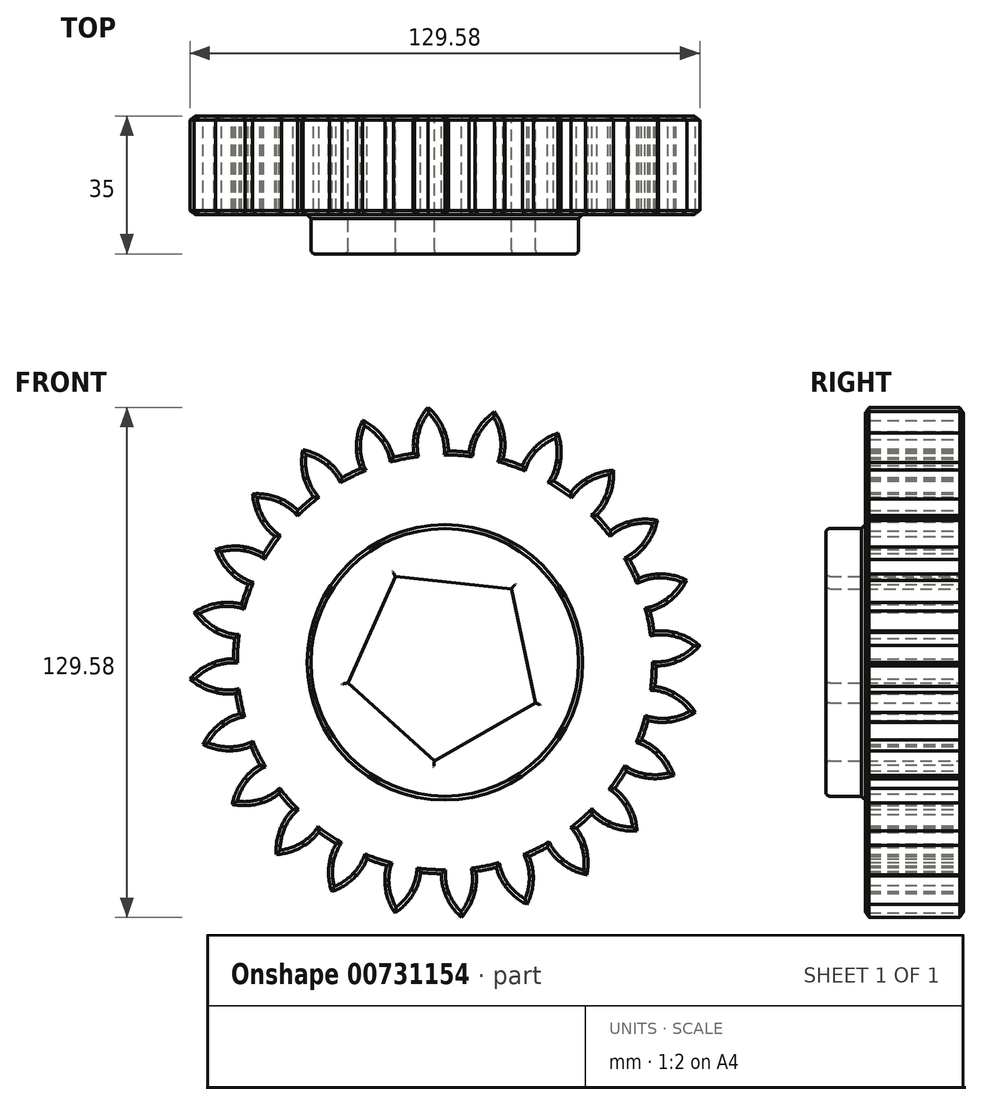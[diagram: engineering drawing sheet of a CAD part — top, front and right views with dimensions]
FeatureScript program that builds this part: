
annotation { "Feature Type Name" : "Feature", "Feature Type Description" : "" }
export const myFeature = defineFeature(function(context is Context, id is Id, definition is map)
    precondition{}
    {
        {
            var Q0;
            Q0=qCreatedBy(makeId("Front.planeOp"),FACE);
            var sketch = newSketch(context, id + "F0", { "sketchPlane" : qUnion([Q0])});
            skCircle(sketch, "E0", {"center": v(0, 0) * mm, "radius": 63.5 * mm, "construction": true});
            skCircle(sketch, "E1", {"center": v(0, 0) * mm, "radius": 58.67 * mm, "construction": true});
            skCircle(sketch, "E2", {"center": v(0, 0) * mm, "radius": 53.72 * mm});
            skLineSegment(sketch, "E3", {"start": v(0, 0) * mm, "end": v(0, 74.51) * mm, "construction": true});
            skLineSegment(sketch, "E4", {"start": v(0, 0) * mm, "end": v(-4.88, 74.51) * mm, "construction": true});
            skLineSegment(sketch, "E5", {"start": v(0, 58.67) * mm, "end": v(-41.54, 58.67) * mm, "construction": true});
            skLineSegment(sketch, "E6", {"start": v(0, 58.67) * mm, "end": v(-41.54, 43.56) * mm, "construction": true});
            skCircle(sketch, "E7", {"center": v(0, 0) * mm, "radius": 55.14 * mm, "construction": true});
            skCircle(sketch, "E8", {"center": v(0, 58.67) * mm, "radius": 14.6 * mm, "construction": true});
            skCircle(sketch, "E9", {"center": v(-13.72, 53.68) * mm, "radius": 14.6 * mm, "construction": true});
            skArc(sketch, "E10", {"start": v(0, 58.67) * mm, "mid": v(-1.73, 62) * mm, "end": v(-4.25, 64.8) * mm});
            skArc(sketch, "E11.MirrorCS", {"start": v(-7.66, 58.17) * mm, "mid": v(-6.38, 61.7) * mm, "end": v(-4.25, 64.8) * mm});
            skArc(sketch, "E12", {"start": v(0.88, 53.71) * mm, "mid": v(0.67, 56.24) * mm, "end": v(0, 58.67) * mm});
            skArc(sketch, "E13.MirrorCS", {"start": v(-7.88, 53.14) * mm, "mid": v(-8, 55.67) * mm, "end": v(-7.66, 58.17) * mm});
            skCircle(sketch, "E14", {"center": v(0, 0) * mm, "radius": 34 * mm});
            skCircle(sketch, "E15.cCircle", {"center": v(0, 0) * mm, "radius": 20.38 * mm, "construction": true});
            skLineSegment(sketch, "E15.0", {"start": v(-12.57, 21.83) * mm, "end": v(16.88, 18.7) * mm});
            skLineSegment(sketch, "E15.1", {"start": v(16.88, 18.7) * mm, "end": v(23, -10.27) * mm});
            skLineSegment(sketch, "E15.2", {"start": v(23, -10.27) * mm, "end": v(-2.66, -25.05) * mm});
            skLineSegment(sketch, "E15.3", {"start": v(-2.66, -25.05) * mm, "end": v(-24.64, -5.2) * mm});
            skLineSegment(sketch, "E15.4", {"start": v(-24.64, -5.2) * mm, "end": v(-12.57, 21.83) * mm});
            skPoint(sketch, "E15.0.midPoint", {"position": v(2.16, 20.26) * mm});
            skSolve(sketch);
        }
        {
            var Q0;
            Q0=makeQuery(id+"F0.imprint","IMPRINT",FACE,{"disambiguationData":[TD([[makeQuery(id+"F0.imprint","IMPRINT",EDGE,{"derivedFrom":sQuery(id+"F0.wireOp",EDGE,"E10")}),1.0]])]});
            var Q1;
            {var subQ0=sQuery(id+"F0.wireOp",EDGE,"E2");var subQ1=makeQuery(id+"F0.imprint","INTERSECT",VERTEX,{"derivedFrom":[subQ0,sQuery(id+"F0.wireOp",EDGE,"E12")]});Q1=makeQuery(id+"F0.imprint","IMPRINT",FACE,{"disambiguationData":[TD([[makeQuery(id+"F0.imprint","IMPRINT",EDGE,{"disambiguationData":[TD([[subQ1,-1.0]])],"derivedFrom":subQ0}),1.0]])]});}
            extrude(context, id + "F1", {"entities" : qUnion([Q0, Q1]), "depth" : 25 * mm, "offsetDistance" : 25 * mm});
        }
        {
            var Q0;
            Q0=makeQuery(id+"F1.opExtrude","SWEPT_BODY",BODY,{"disambiguationData":[OSD([sQuery(id+"F0.wireOp",EDGE,"E2"),sQuery(id+"F0.wireOp",EDGE,"E10"),sQuery(id+"F0.wireOp",EDGE,"E11.MirrorCS"),sQuery(id+"F0.wireOp",EDGE,"E12"),sQuery(id+"F0.wireOp",EDGE,"E13.MirrorCS")])]});
            var Q1;
            Q1=makeQuery(id+"F1.opExtrude","SWEPT_FACE",FACE,{"disambiguationData":[OSD([sQuery(id+"F0.wireOp",EDGE,"E2")])]});
            circularPattern(context, id + "F2", {"entities" : qUnion([Q0]), "axis" : qUnion([Q1]), "angle" : 360 * degree, "instanceCount" : 24, "equalSpace" : true});
        }
        {
            var Q0;
            Q0=makeQuery(id+"F0.imprint","IMPRINT",FACE,{"disambiguationData":[TD([[makeQuery(id+"F0.imprint","IMPRINT",EDGE,{"derivedFrom":sQuery(id+"F0.wireOp",EDGE,"E14")}),1.0]])]});
            extrude(context, id + "F3", {"entities" : qUnion([Q0]), "operationType" : NewBodyOperationType.ADD, "depth" : 35 * mm, "offsetDistance" : 25 * mm});
        }
        {
            var Q0;
            {var subQ0=makeQuery(id+"F1.opExtrude","CAP_FACE",FACE,{"disambiguationData":[OSD([sQuery(id+"F0.wireOp",EDGE,"E2"),sQuery(id+"F0.wireOp",EDGE,"E10"),sQuery(id+"F0.wireOp",EDGE,"E11.MirrorCS"),sQuery(id+"F0.wireOp",EDGE,"E12"),sQuery(id+"F0.wireOp",EDGE,"E13.MirrorCS"),sQuery(id+"F0.wireOp",EDGE,"E14")])],"isStart":false});Q0=makeQuery(id+"F3.boolean.opBoolean","MERGE",FACE,{"derivedFrom":[subQ0,makeQuery(id+"F2.opPattern","COPY",FACE,{"derivedFrom":subQ0,"instanceName":"1"}),makeQuery(id+"F2.opPattern","COPY",FACE,{"derivedFrom":subQ0,"instanceName":"2"}),makeQuery(id+"F2.opPattern","COPY",FACE,{"derivedFrom":subQ0,"instanceName":"3"}),makeQuery(id+"F2.opPattern","COPY",FACE,{"derivedFrom":subQ0,"instanceName":"4"}),makeQuery(id+"F2.opPattern","COPY",FACE,{"derivedFrom":subQ0,"instanceName":"5"}),makeQuery(id+"F2.opPattern","COPY",FACE,{"derivedFrom":subQ0,"instanceName":"6"}),makeQuery(id+"F2.opPattern","COPY",FACE,{"derivedFrom":subQ0,"instanceName":"7"}),makeQuery(id+"F2.opPattern","COPY",FACE,{"derivedFrom":subQ0,"instanceName":"8"}),makeQuery(id+"F2.opPattern","COPY",FACE,{"derivedFrom":subQ0,"instanceName":"9"}),makeQuery(id+"F2.opPattern","COPY",FACE,{"derivedFrom":subQ0,"instanceName":"10"}),makeQuery(id+"F2.opPattern","COPY",FACE,{"derivedFrom":subQ0,"instanceName":"11"}),makeQuery(id+"F2.opPattern","COPY",FACE,{"derivedFrom":subQ0,"instanceName":"12"}),makeQuery(id+"F2.opPattern","COPY",FACE,{"derivedFrom":subQ0,"instanceName":"13"}),makeQuery(id+"F2.opPattern","COPY",FACE,{"derivedFrom":subQ0,"instanceName":"14"}),makeQuery(id+"F2.opPattern","COPY",FACE,{"derivedFrom":subQ0,"instanceName":"15"}),makeQuery(id+"F2.opPattern","COPY",FACE,{"derivedFrom":subQ0,"instanceName":"16"}),makeQuery(id+"F2.opPattern","COPY",FACE,{"derivedFrom":subQ0,"instanceName":"17"}),makeQuery(id+"F2.opPattern","COPY",FACE,{"derivedFrom":subQ0,"instanceName":"18"}),makeQuery(id+"F2.opPattern","COPY",FACE,{"derivedFrom":subQ0,"instanceName":"19"}),makeQuery(id+"F2.opPattern","COPY",FACE,{"derivedFrom":subQ0,"instanceName":"20"}),makeQuery(id+"F2.opPattern","COPY",FACE,{"derivedFrom":subQ0,"instanceName":"21"}),makeQuery(id+"F2.opPattern","COPY",FACE,{"derivedFrom":subQ0,"instanceName":"22"}),makeQuery(id+"F2.opPattern","COPY",FACE,{"derivedFrom":subQ0,"instanceName":"23"})]});}
            var Q1;
            {var subQ0=sQuery(id+"F0.wireOp",EDGE,"E14");var subQ1=makeQuery(id+"F1.opExtrude","CAP_FACE",FACE,{"disambiguationData":[OSD([sQuery(id+"F0.wireOp",EDGE,"E2"),sQuery(id+"F0.wireOp",EDGE,"E10"),sQuery(id+"F0.wireOp",EDGE,"E11.MirrorCS"),sQuery(id+"F0.wireOp",EDGE,"E12"),sQuery(id+"F0.wireOp",EDGE,"E13.MirrorCS"),subQ0])],"isStart":true});Q1=makeQuery(id+"F3.boolean.opBoolean","MERGE",FACE,{"derivedFrom":[subQ1,makeQuery(id+"F2.opPattern","COPY",FACE,{"derivedFrom":subQ1,"instanceName":"1"}),makeQuery(id+"F2.opPattern","COPY",FACE,{"derivedFrom":subQ1,"instanceName":"2"}),makeQuery(id+"F2.opPattern","COPY",FACE,{"derivedFrom":subQ1,"instanceName":"3"}),makeQuery(id+"F2.opPattern","COPY",FACE,{"derivedFrom":subQ1,"instanceName":"4"}),makeQuery(id+"F2.opPattern","COPY",FACE,{"derivedFrom":subQ1,"instanceName":"5"}),makeQuery(id+"F2.opPattern","COPY",FACE,{"derivedFrom":subQ1,"instanceName":"6"}),makeQuery(id+"F2.opPattern","COPY",FACE,{"derivedFrom":subQ1,"instanceName":"7"}),makeQuery(id+"F2.opPattern","COPY",FACE,{"derivedFrom":subQ1,"instanceName":"8"}),makeQuery(id+"F2.opPattern","COPY",FACE,{"derivedFrom":subQ1,"instanceName":"9"}),makeQuery(id+"F2.opPattern","COPY",FACE,{"derivedFrom":subQ1,"instanceName":"10"}),makeQuery(id+"F2.opPattern","COPY",FACE,{"derivedFrom":subQ1,"instanceName":"11"}),makeQuery(id+"F2.opPattern","COPY",FACE,{"derivedFrom":subQ1,"instanceName":"12"}),makeQuery(id+"F2.opPattern","COPY",FACE,{"derivedFrom":subQ1,"instanceName":"13"}),makeQuery(id+"F2.opPattern","COPY",FACE,{"derivedFrom":subQ1,"instanceName":"14"}),makeQuery(id+"F2.opPattern","COPY",FACE,{"derivedFrom":subQ1,"instanceName":"15"}),makeQuery(id+"F2.opPattern","COPY",FACE,{"derivedFrom":subQ1,"instanceName":"16"}),makeQuery(id+"F2.opPattern","COPY",FACE,{"derivedFrom":subQ1,"instanceName":"17"}),makeQuery(id+"F2.opPattern","COPY",FACE,{"derivedFrom":subQ1,"instanceName":"18"}),makeQuery(id+"F2.opPattern","COPY",FACE,{"derivedFrom":subQ1,"instanceName":"19"}),makeQuery(id+"F2.opPattern","COPY",FACE,{"derivedFrom":subQ1,"instanceName":"20"}),makeQuery(id+"F2.opPattern","COPY",FACE,{"derivedFrom":subQ1,"instanceName":"21"}),makeQuery(id+"F2.opPattern","COPY",FACE,{"derivedFrom":subQ1,"instanceName":"22"}),makeQuery(id+"F2.opPattern","COPY",FACE,{"derivedFrom":subQ1,"instanceName":"23"}),makeQuery(id+"F3.opExtrude","CAP_FACE",FACE,{"disambiguationData":[OSD([subQ0,sQuery(id+"F0.wireOp",EDGE,"E15.0"),sQuery(id+"F0.wireOp",EDGE,"E15.1"),sQuery(id+"F0.wireOp",EDGE,"E15.2"),sQuery(id+"F0.wireOp",EDGE,"E15.3"),sQuery(id+"F0.wireOp",EDGE,"E15.4")])],"isStart":true})]});}
            chamfer(context, id + "F4", {"entities" : qUnion([Q0, Q1]), "width" : 1 * mm, "tangentPropagation" : true});
        }
        {
            var Q0;
            {var subQ0=sQuery(id+"F0.wireOp",EDGE,"E15.1");Q0=makeQuery(id+"F4.opChamfer","BLEND_EDGE",EDGE,{"blendedFrom":[makeQuery(id+"F3.opExtrude","CAP_EDGE",EDGE,{"disambiguationData":[OSD([subQ0])],"isStart":true}),makeQuery(id+"F3.opExtrude","SWEPT_FACE",FACE,{"disambiguationData":[OSD([subQ0])]})],"blendedInto":[makeQuery(id+"F3.opExtrude","SWEPT_FACE",FACE,{"disambiguationData":[OSD([subQ0])]})]});}
            var Q1;
            Q1=makeQuery(id+"F3.opExtrude","CAP_FACE",FACE,{"disambiguationData":[OSD([sQuery(id+"F0.wireOp",EDGE,"E14"),sQuery(id+"F0.wireOp",EDGE,"E15.0"),sQuery(id+"F0.wireOp",EDGE,"E15.1"),sQuery(id+"F0.wireOp",EDGE,"E15.2"),sQuery(id+"F0.wireOp",EDGE,"E15.3"),sQuery(id+"F0.wireOp",EDGE,"E15.4")])],"isStart":false});
            var Q2;
            Q2=makeQuery(id+"F3.opExtrude","CAP_EDGE",EDGE,{"disambiguationData":[OSD([sQuery(id+"F0.wireOp",EDGE,"E15.2")])],"isStart":false});
            var Q3;
            Q3=makeQuery(id+"F3.opExtrude","CAP_EDGE",EDGE,{"disambiguationData":[OSD([sQuery(id+"F0.wireOp",EDGE,"E15.3")])],"isStart":false});
            var Q4;
            Q4=makeQuery(id+"F3.opExtrude","CAP_EDGE",EDGE,{"disambiguationData":[OSD([sQuery(id+"F0.wireOp",EDGE,"E15.4")])],"isStart":false});
            var Q5;
            Q5=makeQuery(id+"F3.opExtrude","CAP_EDGE",EDGE,{"disambiguationData":[OSD([sQuery(id+"F0.wireOp",EDGE,"E15.0")])],"isStart":false});
            var Q6;
            {var subQ0=sQuery(id+"F0.wireOp",EDGE,"E15.4");var subQ1=sQuery(id+"F0.wireOp",EDGE,"E14");var subQ2=makeQuery(id+"F1.opExtrude","CAP_FACE",FACE,{"disambiguationData":[OSD([sQuery(id+"F0.wireOp",EDGE,"E2"),sQuery(id+"F0.wireOp",EDGE,"E10"),sQuery(id+"F0.wireOp",EDGE,"E11.MirrorCS"),sQuery(id+"F0.wireOp",EDGE,"E12"),sQuery(id+"F0.wireOp",EDGE,"E13.MirrorCS"),subQ1])],"isStart":true});Q6=makeQuery(id+"F4.opChamfer","BLEND_EDGE",EDGE,{"blendedFrom":[makeQuery(id+"F3.opExtrude","CAP_EDGE",EDGE,{"disambiguationData":[OSD([subQ0])],"isStart":true}),makeQuery(id+"F3.boolean.opBoolean","MERGE",FACE,{"derivedFrom":[subQ2,makeQuery(id+"F2.opPattern","COPY",FACE,{"derivedFrom":subQ2,"instanceName":"1"}),makeQuery(id+"F2.opPattern","COPY",FACE,{"derivedFrom":subQ2,"instanceName":"2"}),makeQuery(id+"F2.opPattern","COPY",FACE,{"derivedFrom":subQ2,"instanceName":"3"}),makeQuery(id+"F2.opPattern","COPY",FACE,{"derivedFrom":subQ2,"instanceName":"4"}),makeQuery(id+"F2.opPattern","COPY",FACE,{"derivedFrom":subQ2,"instanceName":"5"}),makeQuery(id+"F2.opPattern","COPY",FACE,{"derivedFrom":subQ2,"instanceName":"6"}),makeQuery(id+"F2.opPattern","COPY",FACE,{"derivedFrom":subQ2,"instanceName":"7"}),makeQuery(id+"F2.opPattern","COPY",FACE,{"derivedFrom":subQ2,"instanceName":"8"}),makeQuery(id+"F2.opPattern","COPY",FACE,{"derivedFrom":subQ2,"instanceName":"9"}),makeQuery(id+"F2.opPattern","COPY",FACE,{"derivedFrom":subQ2,"instanceName":"10"}),makeQuery(id+"F2.opPattern","COPY",FACE,{"derivedFrom":subQ2,"instanceName":"11"}),makeQuery(id+"F2.opPattern","COPY",FACE,{"derivedFrom":subQ2,"instanceName":"12"}),makeQuery(id+"F2.opPattern","COPY",FACE,{"derivedFrom":subQ2,"instanceName":"13"}),makeQuery(id+"F2.opPattern","COPY",FACE,{"derivedFrom":subQ2,"instanceName":"14"}),makeQuery(id+"F2.opPattern","COPY",FACE,{"derivedFrom":subQ2,"instanceName":"15"}),makeQuery(id+"F2.opPattern","COPY",FACE,{"derivedFrom":subQ2,"instanceName":"16"}),makeQuery(id+"F2.opPattern","COPY",FACE,{"derivedFrom":subQ2,"instanceName":"17"}),makeQuery(id+"F2.opPattern","COPY",FACE,{"derivedFrom":subQ2,"instanceName":"18"}),makeQuery(id+"F2.opPattern","COPY",FACE,{"derivedFrom":subQ2,"instanceName":"19"}),makeQuery(id+"F2.opPattern","COPY",FACE,{"derivedFrom":subQ2,"instanceName":"20"}),makeQuery(id+"F2.opPattern","COPY",FACE,{"derivedFrom":subQ2,"instanceName":"21"}),makeQuery(id+"F2.opPattern","COPY",FACE,{"derivedFrom":subQ2,"instanceName":"22"}),makeQuery(id+"F2.opPattern","COPY",FACE,{"derivedFrom":subQ2,"instanceName":"23"}),makeQuery(id+"F3.opExtrude","CAP_FACE",FACE,{"disambiguationData":[OSD([subQ1,sQuery(id+"F0.wireOp",EDGE,"E15.0"),sQuery(id+"F0.wireOp",EDGE,"E15.1"),sQuery(id+"F0.wireOp",EDGE,"E15.2"),sQuery(id+"F0.wireOp",EDGE,"E15.3"),subQ0])],"isStart":true})]})],"blendedInto":[makeQuery(id+"F3.boolean.opBoolean","MERGE",FACE,{"derivedFrom":[subQ2,makeQuery(id+"F2.opPattern","COPY",FACE,{"derivedFrom":subQ2,"instanceName":"1"}),makeQuery(id+"F2.opPattern","COPY",FACE,{"derivedFrom":subQ2,"instanceName":"2"}),makeQuery(id+"F2.opPattern","COPY",FACE,{"derivedFrom":subQ2,"instanceName":"3"}),makeQuery(id+"F2.opPattern","COPY",FACE,{"derivedFrom":subQ2,"instanceName":"4"}),makeQuery(id+"F2.opPattern","COPY",FACE,{"derivedFrom":subQ2,"instanceName":"5"}),makeQuery(id+"F2.opPattern","COPY",FACE,{"derivedFrom":subQ2,"instanceName":"6"}),makeQuery(id+"F2.opPattern","COPY",FACE,{"derivedFrom":subQ2,"instanceName":"7"}),makeQuery(id+"F2.opPattern","COPY",FACE,{"derivedFrom":subQ2,"instanceName":"8"}),makeQuery(id+"F2.opPattern","COPY",FACE,{"derivedFrom":subQ2,"instanceName":"9"}),makeQuery(id+"F2.opPattern","COPY",FACE,{"derivedFrom":subQ2,"instanceName":"10"}),makeQuery(id+"F2.opPattern","COPY",FACE,{"derivedFrom":subQ2,"instanceName":"11"}),makeQuery(id+"F2.opPattern","COPY",FACE,{"derivedFrom":subQ2,"instanceName":"12"}),makeQuery(id+"F2.opPattern","COPY",FACE,{"derivedFrom":subQ2,"instanceName":"13"}),makeQuery(id+"F2.opPattern","COPY",FACE,{"derivedFrom":subQ2,"instanceName":"14"}),makeQuery(id+"F2.opPattern","COPY",FACE,{"derivedFrom":subQ2,"instanceName":"15"}),makeQuery(id+"F2.opPattern","COPY",FACE,{"derivedFrom":subQ2,"instanceName":"16"}),makeQuery(id+"F2.opPattern","COPY",FACE,{"derivedFrom":subQ2,"instanceName":"17"}),makeQuery(id+"F2.opPattern","COPY",FACE,{"derivedFrom":subQ2,"instanceName":"18"}),makeQuery(id+"F2.opPattern","COPY",FACE,{"derivedFrom":subQ2,"instanceName":"19"}),makeQuery(id+"F2.opPattern","COPY",FACE,{"derivedFrom":subQ2,"instanceName":"20"}),makeQuery(id+"F2.opPattern","COPY",FACE,{"derivedFrom":subQ2,"instanceName":"21"}),makeQuery(id+"F2.opPattern","COPY",FACE,{"derivedFrom":subQ2,"instanceName":"22"}),makeQuery(id+"F2.opPattern","COPY",FACE,{"derivedFrom":subQ2,"instanceName":"23"}),makeQuery(id+"F3.opExtrude","CAP_FACE",FACE,{"disambiguationData":[OSD([subQ1,sQuery(id+"F0.wireOp",EDGE,"E15.0"),sQuery(id+"F0.wireOp",EDGE,"E15.1"),sQuery(id+"F0.wireOp",EDGE,"E15.2"),sQuery(id+"F0.wireOp",EDGE,"E15.3"),subQ0])],"isStart":true})]})]});}
            var Q7;
            {var subQ0=sQuery(id+"F0.wireOp",EDGE,"E15.0");var subQ1=sQuery(id+"F0.wireOp",EDGE,"E14");var subQ2=makeQuery(id+"F1.opExtrude","CAP_FACE",FACE,{"disambiguationData":[OSD([sQuery(id+"F0.wireOp",EDGE,"E2"),sQuery(id+"F0.wireOp",EDGE,"E10"),sQuery(id+"F0.wireOp",EDGE,"E11.MirrorCS"),sQuery(id+"F0.wireOp",EDGE,"E12"),sQuery(id+"F0.wireOp",EDGE,"E13.MirrorCS"),subQ1])],"isStart":true});Q7=makeQuery(id+"F4.opChamfer","BLEND_EDGE",EDGE,{"blendedFrom":[makeQuery(id+"F3.opExtrude","CAP_EDGE",EDGE,{"disambiguationData":[OSD([subQ0])],"isStart":true}),makeQuery(id+"F3.boolean.opBoolean","MERGE",FACE,{"derivedFrom":[subQ2,makeQuery(id+"F2.opPattern","COPY",FACE,{"derivedFrom":subQ2,"instanceName":"1"}),makeQuery(id+"F2.opPattern","COPY",FACE,{"derivedFrom":subQ2,"instanceName":"2"}),makeQuery(id+"F2.opPattern","COPY",FACE,{"derivedFrom":subQ2,"instanceName":"3"}),makeQuery(id+"F2.opPattern","COPY",FACE,{"derivedFrom":subQ2,"instanceName":"4"}),makeQuery(id+"F2.opPattern","COPY",FACE,{"derivedFrom":subQ2,"instanceName":"5"}),makeQuery(id+"F2.opPattern","COPY",FACE,{"derivedFrom":subQ2,"instanceName":"6"}),makeQuery(id+"F2.opPattern","COPY",FACE,{"derivedFrom":subQ2,"instanceName":"7"}),makeQuery(id+"F2.opPattern","COPY",FACE,{"derivedFrom":subQ2,"instanceName":"8"}),makeQuery(id+"F2.opPattern","COPY",FACE,{"derivedFrom":subQ2,"instanceName":"9"}),makeQuery(id+"F2.opPattern","COPY",FACE,{"derivedFrom":subQ2,"instanceName":"10"}),makeQuery(id+"F2.opPattern","COPY",FACE,{"derivedFrom":subQ2,"instanceName":"11"}),makeQuery(id+"F2.opPattern","COPY",FACE,{"derivedFrom":subQ2,"instanceName":"12"}),makeQuery(id+"F2.opPattern","COPY",FACE,{"derivedFrom":subQ2,"instanceName":"13"}),makeQuery(id+"F2.opPattern","COPY",FACE,{"derivedFrom":subQ2,"instanceName":"14"}),makeQuery(id+"F2.opPattern","COPY",FACE,{"derivedFrom":subQ2,"instanceName":"15"}),makeQuery(id+"F2.opPattern","COPY",FACE,{"derivedFrom":subQ2,"instanceName":"16"}),makeQuery(id+"F2.opPattern","COPY",FACE,{"derivedFrom":subQ2,"instanceName":"17"}),makeQuery(id+"F2.opPattern","COPY",FACE,{"derivedFrom":subQ2,"instanceName":"18"}),makeQuery(id+"F2.opPattern","COPY",FACE,{"derivedFrom":subQ2,"instanceName":"19"}),makeQuery(id+"F2.opPattern","COPY",FACE,{"derivedFrom":subQ2,"instanceName":"20"}),makeQuery(id+"F2.opPattern","COPY",FACE,{"derivedFrom":subQ2,"instanceName":"21"}),makeQuery(id+"F2.opPattern","COPY",FACE,{"derivedFrom":subQ2,"instanceName":"22"}),makeQuery(id+"F2.opPattern","COPY",FACE,{"derivedFrom":subQ2,"instanceName":"23"}),makeQuery(id+"F3.opExtrude","CAP_FACE",FACE,{"disambiguationData":[OSD([subQ1,subQ0,sQuery(id+"F0.wireOp",EDGE,"E15.1"),sQuery(id+"F0.wireOp",EDGE,"E15.2"),sQuery(id+"F0.wireOp",EDGE,"E15.3"),sQuery(id+"F0.wireOp",EDGE,"E15.4")])],"isStart":true})]})],"blendedInto":[makeQuery(id+"F3.boolean.opBoolean","MERGE",FACE,{"derivedFrom":[subQ2,makeQuery(id+"F2.opPattern","COPY",FACE,{"derivedFrom":subQ2,"instanceName":"1"}),makeQuery(id+"F2.opPattern","COPY",FACE,{"derivedFrom":subQ2,"instanceName":"2"}),makeQuery(id+"F2.opPattern","COPY",FACE,{"derivedFrom":subQ2,"instanceName":"3"}),makeQuery(id+"F2.opPattern","COPY",FACE,{"derivedFrom":subQ2,"instanceName":"4"}),makeQuery(id+"F2.opPattern","COPY",FACE,{"derivedFrom":subQ2,"instanceName":"5"}),makeQuery(id+"F2.opPattern","COPY",FACE,{"derivedFrom":subQ2,"instanceName":"6"}),makeQuery(id+"F2.opPattern","COPY",FACE,{"derivedFrom":subQ2,"instanceName":"7"}),makeQuery(id+"F2.opPattern","COPY",FACE,{"derivedFrom":subQ2,"instanceName":"8"}),makeQuery(id+"F2.opPattern","COPY",FACE,{"derivedFrom":subQ2,"instanceName":"9"}),makeQuery(id+"F2.opPattern","COPY",FACE,{"derivedFrom":subQ2,"instanceName":"10"}),makeQuery(id+"F2.opPattern","COPY",FACE,{"derivedFrom":subQ2,"instanceName":"11"}),makeQuery(id+"F2.opPattern","COPY",FACE,{"derivedFrom":subQ2,"instanceName":"12"}),makeQuery(id+"F2.opPattern","COPY",FACE,{"derivedFrom":subQ2,"instanceName":"13"}),makeQuery(id+"F2.opPattern","COPY",FACE,{"derivedFrom":subQ2,"instanceName":"14"}),makeQuery(id+"F2.opPattern","COPY",FACE,{"derivedFrom":subQ2,"instanceName":"15"}),makeQuery(id+"F2.opPattern","COPY",FACE,{"derivedFrom":subQ2,"instanceName":"16"}),makeQuery(id+"F2.opPattern","COPY",FACE,{"derivedFrom":subQ2,"instanceName":"17"}),makeQuery(id+"F2.opPattern","COPY",FACE,{"derivedFrom":subQ2,"instanceName":"18"}),makeQuery(id+"F2.opPattern","COPY",FACE,{"derivedFrom":subQ2,"instanceName":"19"}),makeQuery(id+"F2.opPattern","COPY",FACE,{"derivedFrom":subQ2,"instanceName":"20"}),makeQuery(id+"F2.opPattern","COPY",FACE,{"derivedFrom":subQ2,"instanceName":"21"}),makeQuery(id+"F2.opPattern","COPY",FACE,{"derivedFrom":subQ2,"instanceName":"22"}),makeQuery(id+"F2.opPattern","COPY",FACE,{"derivedFrom":subQ2,"instanceName":"23"}),makeQuery(id+"F3.opExtrude","CAP_FACE",FACE,{"disambiguationData":[OSD([subQ1,subQ0,sQuery(id+"F0.wireOp",EDGE,"E15.1"),sQuery(id+"F0.wireOp",EDGE,"E15.2"),sQuery(id+"F0.wireOp",EDGE,"E15.3"),sQuery(id+"F0.wireOp",EDGE,"E15.4")])],"isStart":true})]})]});}
            var Q8;
            {var subQ0=sQuery(id+"F0.wireOp",EDGE,"E15.1");var subQ1=sQuery(id+"F0.wireOp",EDGE,"E14");var subQ2=makeQuery(id+"F1.opExtrude","CAP_FACE",FACE,{"disambiguationData":[OSD([sQuery(id+"F0.wireOp",EDGE,"E2"),sQuery(id+"F0.wireOp",EDGE,"E10"),sQuery(id+"F0.wireOp",EDGE,"E11.MirrorCS"),sQuery(id+"F0.wireOp",EDGE,"E12"),sQuery(id+"F0.wireOp",EDGE,"E13.MirrorCS"),subQ1])],"isStart":true});Q8=makeQuery(id+"F4.opChamfer","BLEND_EDGE",EDGE,{"blendedFrom":[makeQuery(id+"F3.opExtrude","CAP_EDGE",EDGE,{"disambiguationData":[OSD([subQ0])],"isStart":true}),makeQuery(id+"F3.boolean.opBoolean","MERGE",FACE,{"derivedFrom":[subQ2,makeQuery(id+"F2.opPattern","COPY",FACE,{"derivedFrom":subQ2,"instanceName":"1"}),makeQuery(id+"F2.opPattern","COPY",FACE,{"derivedFrom":subQ2,"instanceName":"2"}),makeQuery(id+"F2.opPattern","COPY",FACE,{"derivedFrom":subQ2,"instanceName":"3"}),makeQuery(id+"F2.opPattern","COPY",FACE,{"derivedFrom":subQ2,"instanceName":"4"}),makeQuery(id+"F2.opPattern","COPY",FACE,{"derivedFrom":subQ2,"instanceName":"5"}),makeQuery(id+"F2.opPattern","COPY",FACE,{"derivedFrom":subQ2,"instanceName":"6"}),makeQuery(id+"F2.opPattern","COPY",FACE,{"derivedFrom":subQ2,"instanceName":"7"}),makeQuery(id+"F2.opPattern","COPY",FACE,{"derivedFrom":subQ2,"instanceName":"8"}),makeQuery(id+"F2.opPattern","COPY",FACE,{"derivedFrom":subQ2,"instanceName":"9"}),makeQuery(id+"F2.opPattern","COPY",FACE,{"derivedFrom":subQ2,"instanceName":"10"}),makeQuery(id+"F2.opPattern","COPY",FACE,{"derivedFrom":subQ2,"instanceName":"11"}),makeQuery(id+"F2.opPattern","COPY",FACE,{"derivedFrom":subQ2,"instanceName":"12"}),makeQuery(id+"F2.opPattern","COPY",FACE,{"derivedFrom":subQ2,"instanceName":"13"}),makeQuery(id+"F2.opPattern","COPY",FACE,{"derivedFrom":subQ2,"instanceName":"14"}),makeQuery(id+"F2.opPattern","COPY",FACE,{"derivedFrom":subQ2,"instanceName":"15"}),makeQuery(id+"F2.opPattern","COPY",FACE,{"derivedFrom":subQ2,"instanceName":"16"}),makeQuery(id+"F2.opPattern","COPY",FACE,{"derivedFrom":subQ2,"instanceName":"17"}),makeQuery(id+"F2.opPattern","COPY",FACE,{"derivedFrom":subQ2,"instanceName":"18"}),makeQuery(id+"F2.opPattern","COPY",FACE,{"derivedFrom":subQ2,"instanceName":"19"}),makeQuery(id+"F2.opPattern","COPY",FACE,{"derivedFrom":subQ2,"instanceName":"20"}),makeQuery(id+"F2.opPattern","COPY",FACE,{"derivedFrom":subQ2,"instanceName":"21"}),makeQuery(id+"F2.opPattern","COPY",FACE,{"derivedFrom":subQ2,"instanceName":"22"}),makeQuery(id+"F2.opPattern","COPY",FACE,{"derivedFrom":subQ2,"instanceName":"23"}),makeQuery(id+"F3.opExtrude","CAP_FACE",FACE,{"disambiguationData":[OSD([subQ1,sQuery(id+"F0.wireOp",EDGE,"E15.0"),subQ0,sQuery(id+"F0.wireOp",EDGE,"E15.2"),sQuery(id+"F0.wireOp",EDGE,"E15.3"),sQuery(id+"F0.wireOp",EDGE,"E15.4")])],"isStart":true})]})],"blendedInto":[makeQuery(id+"F3.boolean.opBoolean","MERGE",FACE,{"derivedFrom":[subQ2,makeQuery(id+"F2.opPattern","COPY",FACE,{"derivedFrom":subQ2,"instanceName":"1"}),makeQuery(id+"F2.opPattern","COPY",FACE,{"derivedFrom":subQ2,"instanceName":"2"}),makeQuery(id+"F2.opPattern","COPY",FACE,{"derivedFrom":subQ2,"instanceName":"3"}),makeQuery(id+"F2.opPattern","COPY",FACE,{"derivedFrom":subQ2,"instanceName":"4"}),makeQuery(id+"F2.opPattern","COPY",FACE,{"derivedFrom":subQ2,"instanceName":"5"}),makeQuery(id+"F2.opPattern","COPY",FACE,{"derivedFrom":subQ2,"instanceName":"6"}),makeQuery(id+"F2.opPattern","COPY",FACE,{"derivedFrom":subQ2,"instanceName":"7"}),makeQuery(id+"F2.opPattern","COPY",FACE,{"derivedFrom":subQ2,"instanceName":"8"}),makeQuery(id+"F2.opPattern","COPY",FACE,{"derivedFrom":subQ2,"instanceName":"9"}),makeQuery(id+"F2.opPattern","COPY",FACE,{"derivedFrom":subQ2,"instanceName":"10"}),makeQuery(id+"F2.opPattern","COPY",FACE,{"derivedFrom":subQ2,"instanceName":"11"}),makeQuery(id+"F2.opPattern","COPY",FACE,{"derivedFrom":subQ2,"instanceName":"12"}),makeQuery(id+"F2.opPattern","COPY",FACE,{"derivedFrom":subQ2,"instanceName":"13"}),makeQuery(id+"F2.opPattern","COPY",FACE,{"derivedFrom":subQ2,"instanceName":"14"}),makeQuery(id+"F2.opPattern","COPY",FACE,{"derivedFrom":subQ2,"instanceName":"15"}),makeQuery(id+"F2.opPattern","COPY",FACE,{"derivedFrom":subQ2,"instanceName":"16"}),makeQuery(id+"F2.opPattern","COPY",FACE,{"derivedFrom":subQ2,"instanceName":"17"}),makeQuery(id+"F2.opPattern","COPY",FACE,{"derivedFrom":subQ2,"instanceName":"18"}),makeQuery(id+"F2.opPattern","COPY",FACE,{"derivedFrom":subQ2,"instanceName":"19"}),makeQuery(id+"F2.opPattern","COPY",FACE,{"derivedFrom":subQ2,"instanceName":"20"}),makeQuery(id+"F2.opPattern","COPY",FACE,{"derivedFrom":subQ2,"instanceName":"21"}),makeQuery(id+"F2.opPattern","COPY",FACE,{"derivedFrom":subQ2,"instanceName":"22"}),makeQuery(id+"F2.opPattern","COPY",FACE,{"derivedFrom":subQ2,"instanceName":"23"}),makeQuery(id+"F3.opExtrude","CAP_FACE",FACE,{"disambiguationData":[OSD([subQ1,sQuery(id+"F0.wireOp",EDGE,"E15.0"),subQ0,sQuery(id+"F0.wireOp",EDGE,"E15.2"),sQuery(id+"F0.wireOp",EDGE,"E15.3"),sQuery(id+"F0.wireOp",EDGE,"E15.4")])],"isStart":true})]})]});}
            var Q9;
            {var subQ0=sQuery(id+"F0.wireOp",EDGE,"E15.2");var subQ1=sQuery(id+"F0.wireOp",EDGE,"E14");var subQ2=makeQuery(id+"F1.opExtrude","CAP_FACE",FACE,{"disambiguationData":[OSD([sQuery(id+"F0.wireOp",EDGE,"E2"),sQuery(id+"F0.wireOp",EDGE,"E10"),sQuery(id+"F0.wireOp",EDGE,"E11.MirrorCS"),sQuery(id+"F0.wireOp",EDGE,"E12"),sQuery(id+"F0.wireOp",EDGE,"E13.MirrorCS"),subQ1])],"isStart":true});Q9=makeQuery(id+"F4.opChamfer","BLEND_EDGE",EDGE,{"blendedFrom":[makeQuery(id+"F3.opExtrude","CAP_EDGE",EDGE,{"disambiguationData":[OSD([subQ0])],"isStart":true}),makeQuery(id+"F3.boolean.opBoolean","MERGE",FACE,{"derivedFrom":[subQ2,makeQuery(id+"F2.opPattern","COPY",FACE,{"derivedFrom":subQ2,"instanceName":"1"}),makeQuery(id+"F2.opPattern","COPY",FACE,{"derivedFrom":subQ2,"instanceName":"2"}),makeQuery(id+"F2.opPattern","COPY",FACE,{"derivedFrom":subQ2,"instanceName":"3"}),makeQuery(id+"F2.opPattern","COPY",FACE,{"derivedFrom":subQ2,"instanceName":"4"}),makeQuery(id+"F2.opPattern","COPY",FACE,{"derivedFrom":subQ2,"instanceName":"5"}),makeQuery(id+"F2.opPattern","COPY",FACE,{"derivedFrom":subQ2,"instanceName":"6"}),makeQuery(id+"F2.opPattern","COPY",FACE,{"derivedFrom":subQ2,"instanceName":"7"}),makeQuery(id+"F2.opPattern","COPY",FACE,{"derivedFrom":subQ2,"instanceName":"8"}),makeQuery(id+"F2.opPattern","COPY",FACE,{"derivedFrom":subQ2,"instanceName":"9"}),makeQuery(id+"F2.opPattern","COPY",FACE,{"derivedFrom":subQ2,"instanceName":"10"}),makeQuery(id+"F2.opPattern","COPY",FACE,{"derivedFrom":subQ2,"instanceName":"11"}),makeQuery(id+"F2.opPattern","COPY",FACE,{"derivedFrom":subQ2,"instanceName":"12"}),makeQuery(id+"F2.opPattern","COPY",FACE,{"derivedFrom":subQ2,"instanceName":"13"}),makeQuery(id+"F2.opPattern","COPY",FACE,{"derivedFrom":subQ2,"instanceName":"14"}),makeQuery(id+"F2.opPattern","COPY",FACE,{"derivedFrom":subQ2,"instanceName":"15"}),makeQuery(id+"F2.opPattern","COPY",FACE,{"derivedFrom":subQ2,"instanceName":"16"}),makeQuery(id+"F2.opPattern","COPY",FACE,{"derivedFrom":subQ2,"instanceName":"17"}),makeQuery(id+"F2.opPattern","COPY",FACE,{"derivedFrom":subQ2,"instanceName":"18"}),makeQuery(id+"F2.opPattern","COPY",FACE,{"derivedFrom":subQ2,"instanceName":"19"}),makeQuery(id+"F2.opPattern","COPY",FACE,{"derivedFrom":subQ2,"instanceName":"20"}),makeQuery(id+"F2.opPattern","COPY",FACE,{"derivedFrom":subQ2,"instanceName":"21"}),makeQuery(id+"F2.opPattern","COPY",FACE,{"derivedFrom":subQ2,"instanceName":"22"}),makeQuery(id+"F2.opPattern","COPY",FACE,{"derivedFrom":subQ2,"instanceName":"23"}),makeQuery(id+"F3.opExtrude","CAP_FACE",FACE,{"disambiguationData":[OSD([subQ1,sQuery(id+"F0.wireOp",EDGE,"E15.0"),sQuery(id+"F0.wireOp",EDGE,"E15.1"),subQ0,sQuery(id+"F0.wireOp",EDGE,"E15.3"),sQuery(id+"F0.wireOp",EDGE,"E15.4")])],"isStart":true})]})],"blendedInto":[makeQuery(id+"F3.boolean.opBoolean","MERGE",FACE,{"derivedFrom":[subQ2,makeQuery(id+"F2.opPattern","COPY",FACE,{"derivedFrom":subQ2,"instanceName":"1"}),makeQuery(id+"F2.opPattern","COPY",FACE,{"derivedFrom":subQ2,"instanceName":"2"}),makeQuery(id+"F2.opPattern","COPY",FACE,{"derivedFrom":subQ2,"instanceName":"3"}),makeQuery(id+"F2.opPattern","COPY",FACE,{"derivedFrom":subQ2,"instanceName":"4"}),makeQuery(id+"F2.opPattern","COPY",FACE,{"derivedFrom":subQ2,"instanceName":"5"}),makeQuery(id+"F2.opPattern","COPY",FACE,{"derivedFrom":subQ2,"instanceName":"6"}),makeQuery(id+"F2.opPattern","COPY",FACE,{"derivedFrom":subQ2,"instanceName":"7"}),makeQuery(id+"F2.opPattern","COPY",FACE,{"derivedFrom":subQ2,"instanceName":"8"}),makeQuery(id+"F2.opPattern","COPY",FACE,{"derivedFrom":subQ2,"instanceName":"9"}),makeQuery(id+"F2.opPattern","COPY",FACE,{"derivedFrom":subQ2,"instanceName":"10"}),makeQuery(id+"F2.opPattern","COPY",FACE,{"derivedFrom":subQ2,"instanceName":"11"}),makeQuery(id+"F2.opPattern","COPY",FACE,{"derivedFrom":subQ2,"instanceName":"12"}),makeQuery(id+"F2.opPattern","COPY",FACE,{"derivedFrom":subQ2,"instanceName":"13"}),makeQuery(id+"F2.opPattern","COPY",FACE,{"derivedFrom":subQ2,"instanceName":"14"}),makeQuery(id+"F2.opPattern","COPY",FACE,{"derivedFrom":subQ2,"instanceName":"15"}),makeQuery(id+"F2.opPattern","COPY",FACE,{"derivedFrom":subQ2,"instanceName":"16"}),makeQuery(id+"F2.opPattern","COPY",FACE,{"derivedFrom":subQ2,"instanceName":"17"}),makeQuery(id+"F2.opPattern","COPY",FACE,{"derivedFrom":subQ2,"instanceName":"18"}),makeQuery(id+"F2.opPattern","COPY",FACE,{"derivedFrom":subQ2,"instanceName":"19"}),makeQuery(id+"F2.opPattern","COPY",FACE,{"derivedFrom":subQ2,"instanceName":"20"}),makeQuery(id+"F2.opPattern","COPY",FACE,{"derivedFrom":subQ2,"instanceName":"21"}),makeQuery(id+"F2.opPattern","COPY",FACE,{"derivedFrom":subQ2,"instanceName":"22"}),makeQuery(id+"F2.opPattern","COPY",FACE,{"derivedFrom":subQ2,"instanceName":"23"}),makeQuery(id+"F3.opExtrude","CAP_FACE",FACE,{"disambiguationData":[OSD([subQ1,sQuery(id+"F0.wireOp",EDGE,"E15.0"),sQuery(id+"F0.wireOp",EDGE,"E15.1"),subQ0,sQuery(id+"F0.wireOp",EDGE,"E15.3"),sQuery(id+"F0.wireOp",EDGE,"E15.4")])],"isStart":true})]})]});}
            var Q10;
            {var subQ0=sQuery(id+"F0.wireOp",EDGE,"E15.3");var subQ1=sQuery(id+"F0.wireOp",EDGE,"E14");var subQ2=makeQuery(id+"F1.opExtrude","CAP_FACE",FACE,{"disambiguationData":[OSD([sQuery(id+"F0.wireOp",EDGE,"E2"),sQuery(id+"F0.wireOp",EDGE,"E10"),sQuery(id+"F0.wireOp",EDGE,"E11.MirrorCS"),sQuery(id+"F0.wireOp",EDGE,"E12"),sQuery(id+"F0.wireOp",EDGE,"E13.MirrorCS"),subQ1])],"isStart":true});Q10=makeQuery(id+"F4.opChamfer","BLEND_EDGE",EDGE,{"blendedFrom":[makeQuery(id+"F3.opExtrude","CAP_EDGE",EDGE,{"disambiguationData":[OSD([subQ0])],"isStart":true}),makeQuery(id+"F3.boolean.opBoolean","MERGE",FACE,{"derivedFrom":[subQ2,makeQuery(id+"F2.opPattern","COPY",FACE,{"derivedFrom":subQ2,"instanceName":"1"}),makeQuery(id+"F2.opPattern","COPY",FACE,{"derivedFrom":subQ2,"instanceName":"2"}),makeQuery(id+"F2.opPattern","COPY",FACE,{"derivedFrom":subQ2,"instanceName":"3"}),makeQuery(id+"F2.opPattern","COPY",FACE,{"derivedFrom":subQ2,"instanceName":"4"}),makeQuery(id+"F2.opPattern","COPY",FACE,{"derivedFrom":subQ2,"instanceName":"5"}),makeQuery(id+"F2.opPattern","COPY",FACE,{"derivedFrom":subQ2,"instanceName":"6"}),makeQuery(id+"F2.opPattern","COPY",FACE,{"derivedFrom":subQ2,"instanceName":"7"}),makeQuery(id+"F2.opPattern","COPY",FACE,{"derivedFrom":subQ2,"instanceName":"8"}),makeQuery(id+"F2.opPattern","COPY",FACE,{"derivedFrom":subQ2,"instanceName":"9"}),makeQuery(id+"F2.opPattern","COPY",FACE,{"derivedFrom":subQ2,"instanceName":"10"}),makeQuery(id+"F2.opPattern","COPY",FACE,{"derivedFrom":subQ2,"instanceName":"11"}),makeQuery(id+"F2.opPattern","COPY",FACE,{"derivedFrom":subQ2,"instanceName":"12"}),makeQuery(id+"F2.opPattern","COPY",FACE,{"derivedFrom":subQ2,"instanceName":"13"}),makeQuery(id+"F2.opPattern","COPY",FACE,{"derivedFrom":subQ2,"instanceName":"14"}),makeQuery(id+"F2.opPattern","COPY",FACE,{"derivedFrom":subQ2,"instanceName":"15"}),makeQuery(id+"F2.opPattern","COPY",FACE,{"derivedFrom":subQ2,"instanceName":"16"}),makeQuery(id+"F2.opPattern","COPY",FACE,{"derivedFrom":subQ2,"instanceName":"17"}),makeQuery(id+"F2.opPattern","COPY",FACE,{"derivedFrom":subQ2,"instanceName":"18"}),makeQuery(id+"F2.opPattern","COPY",FACE,{"derivedFrom":subQ2,"instanceName":"19"}),makeQuery(id+"F2.opPattern","COPY",FACE,{"derivedFrom":subQ2,"instanceName":"20"}),makeQuery(id+"F2.opPattern","COPY",FACE,{"derivedFrom":subQ2,"instanceName":"21"}),makeQuery(id+"F2.opPattern","COPY",FACE,{"derivedFrom":subQ2,"instanceName":"22"}),makeQuery(id+"F2.opPattern","COPY",FACE,{"derivedFrom":subQ2,"instanceName":"23"}),makeQuery(id+"F3.opExtrude","CAP_FACE",FACE,{"disambiguationData":[OSD([subQ1,sQuery(id+"F0.wireOp",EDGE,"E15.0"),sQuery(id+"F0.wireOp",EDGE,"E15.1"),sQuery(id+"F0.wireOp",EDGE,"E15.2"),subQ0,sQuery(id+"F0.wireOp",EDGE,"E15.4")])],"isStart":true})]})],"blendedInto":[makeQuery(id+"F3.boolean.opBoolean","MERGE",FACE,{"derivedFrom":[subQ2,makeQuery(id+"F2.opPattern","COPY",FACE,{"derivedFrom":subQ2,"instanceName":"1"}),makeQuery(id+"F2.opPattern","COPY",FACE,{"derivedFrom":subQ2,"instanceName":"2"}),makeQuery(id+"F2.opPattern","COPY",FACE,{"derivedFrom":subQ2,"instanceName":"3"}),makeQuery(id+"F2.opPattern","COPY",FACE,{"derivedFrom":subQ2,"instanceName":"4"}),makeQuery(id+"F2.opPattern","COPY",FACE,{"derivedFrom":subQ2,"instanceName":"5"}),makeQuery(id+"F2.opPattern","COPY",FACE,{"derivedFrom":subQ2,"instanceName":"6"}),makeQuery(id+"F2.opPattern","COPY",FACE,{"derivedFrom":subQ2,"instanceName":"7"}),makeQuery(id+"F2.opPattern","COPY",FACE,{"derivedFrom":subQ2,"instanceName":"8"}),makeQuery(id+"F2.opPattern","COPY",FACE,{"derivedFrom":subQ2,"instanceName":"9"}),makeQuery(id+"F2.opPattern","COPY",FACE,{"derivedFrom":subQ2,"instanceName":"10"}),makeQuery(id+"F2.opPattern","COPY",FACE,{"derivedFrom":subQ2,"instanceName":"11"}),makeQuery(id+"F2.opPattern","COPY",FACE,{"derivedFrom":subQ2,"instanceName":"12"}),makeQuery(id+"F2.opPattern","COPY",FACE,{"derivedFrom":subQ2,"instanceName":"13"}),makeQuery(id+"F2.opPattern","COPY",FACE,{"derivedFrom":subQ2,"instanceName":"14"}),makeQuery(id+"F2.opPattern","COPY",FACE,{"derivedFrom":subQ2,"instanceName":"15"}),makeQuery(id+"F2.opPattern","COPY",FACE,{"derivedFrom":subQ2,"instanceName":"16"}),makeQuery(id+"F2.opPattern","COPY",FACE,{"derivedFrom":subQ2,"instanceName":"17"}),makeQuery(id+"F2.opPattern","COPY",FACE,{"derivedFrom":subQ2,"instanceName":"18"}),makeQuery(id+"F2.opPattern","COPY",FACE,{"derivedFrom":subQ2,"instanceName":"19"}),makeQuery(id+"F2.opPattern","COPY",FACE,{"derivedFrom":subQ2,"instanceName":"20"}),makeQuery(id+"F2.opPattern","COPY",FACE,{"derivedFrom":subQ2,"instanceName":"21"}),makeQuery(id+"F2.opPattern","COPY",FACE,{"derivedFrom":subQ2,"instanceName":"22"}),makeQuery(id+"F2.opPattern","COPY",FACE,{"derivedFrom":subQ2,"instanceName":"23"}),makeQuery(id+"F3.opExtrude","CAP_FACE",FACE,{"disambiguationData":[OSD([subQ1,sQuery(id+"F0.wireOp",EDGE,"E15.0"),sQuery(id+"F0.wireOp",EDGE,"E15.1"),sQuery(id+"F0.wireOp",EDGE,"E15.2"),subQ0,sQuery(id+"F0.wireOp",EDGE,"E15.4")])],"isStart":true})]})]});}
            fillet(context, id + "F5", {"entities" : qUnion([Q0, Q1, Q2, Q3, Q4, Q5, Q6, Q7, Q8, Q9, Q10]), "radius" : 1 * mm, "tangentPropagation" : true, "allowEdgeOverflow" : false});
        }
    });
